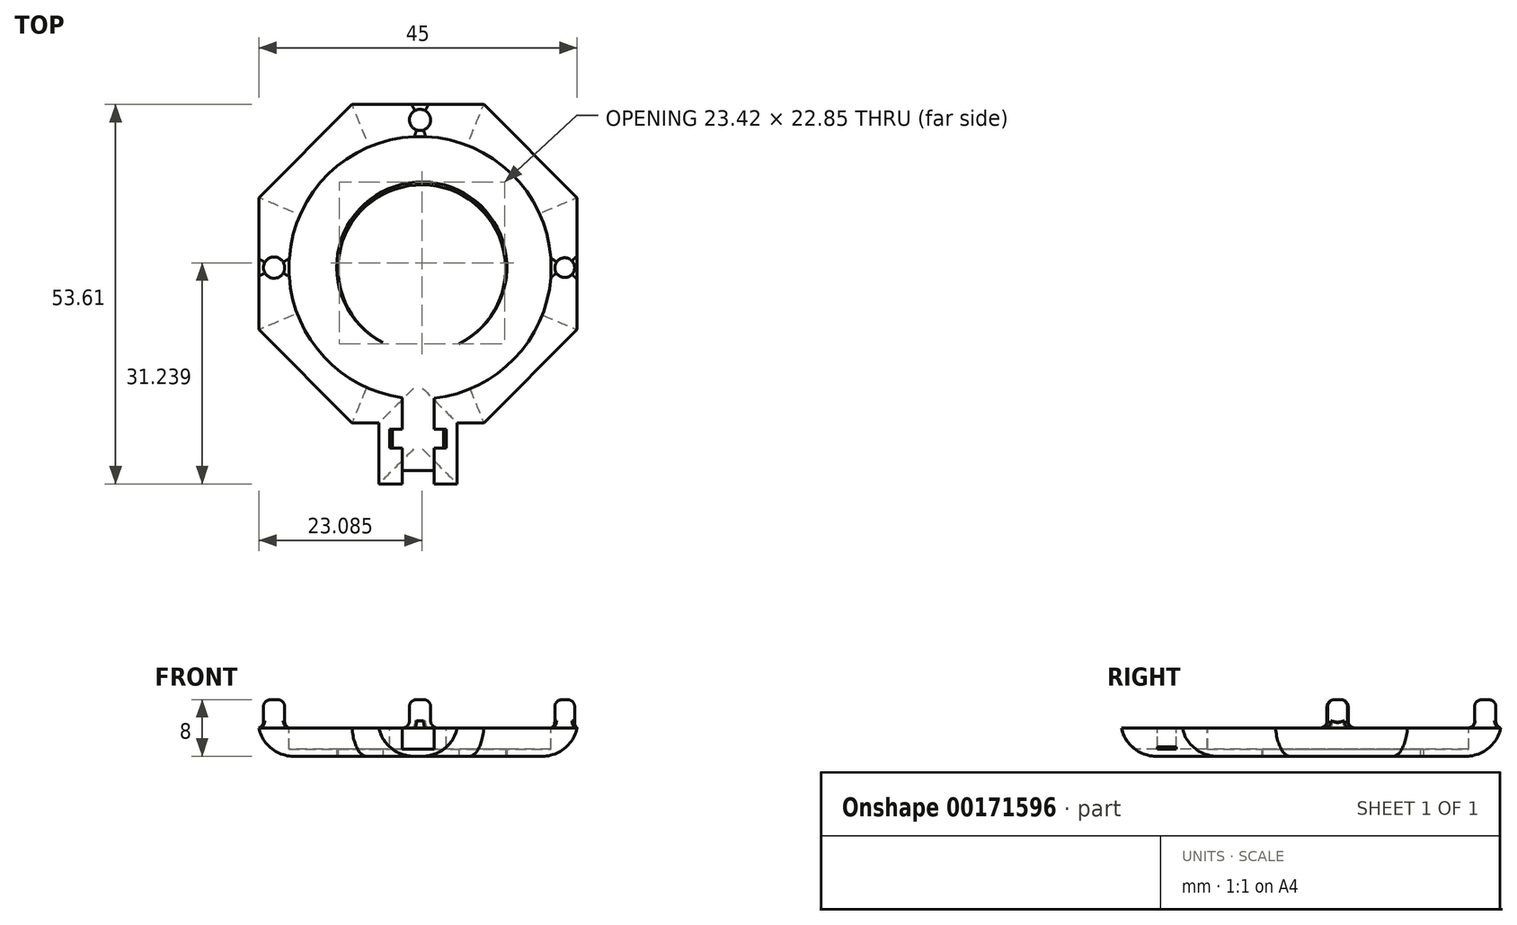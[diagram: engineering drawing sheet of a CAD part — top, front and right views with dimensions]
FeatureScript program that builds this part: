
annotation { "Feature Type Name" : "Feature", "Feature Type Description" : "" }
export const myFeature = defineFeature(function(context is Context, id is Id, definition is map)
    precondition{}
    {
        {
            var Q0;
            Q0=qCreatedBy(makeId("Top.planeOp"),FACE);
            var sketch = newSketch(context, id + "F0", { "sketchPlane" : qUnion([Q0])});
            skCircle(sketch, "E0.cCircle", {"center": v(-0.3, 0.57) * mm, "radius": 22.5 * mm, "construction": true});
            skLineSegment(sketch, "E0.0", {"start": v(9.02, -21.93) * mm, "end": v(-9.62, -21.93) * mm});
            skLineSegment(sketch, "E0.1", {"start": v(-9.62, -21.93) * mm, "end": v(-22.8, -8.75) * mm});
            skLineSegment(sketch, "E0.2", {"start": v(-22.8, -8.75) * mm, "end": v(-22.8, 9.9) * mm});
            skLineSegment(sketch, "E0.3", {"start": v(-22.8, 9.9) * mm, "end": v(-9.62, 23.07) * mm});
            skLineSegment(sketch, "E0.4", {"start": v(-9.62, 23.07) * mm, "end": v(9.02, 23.07) * mm});
            skLineSegment(sketch, "E0.5", {"start": v(9.02, 23.07) * mm, "end": v(22.2, 9.9) * mm});
            skLineSegment(sketch, "E0.6", {"start": v(22.2, 9.9) * mm, "end": v(22.2, -8.75) * mm});
            skLineSegment(sketch, "E0.7", {"start": v(22.2, -8.75) * mm, "end": v(9.02, -21.93) * mm});
            skPoint(sketch, "E0.0.midPoint", {"position": v(-0.3, -21.93) * mm});
            skLineSegment(sketch, "E1", {"start": v(5.26, -21.93) * mm, "end": v(5.26, -30.54) * mm});
            skLineSegment(sketch, "E2", {"start": v(5.26, -30.54) * mm, "end": v(-5.8, -30.54) * mm});
            skLineSegment(sketch, "E3", {"start": v(-5.8, -30.54) * mm, "end": v(-5.8, -21.93) * mm});
            skSolve(sketch);
        }
        {
            var Q0;
            Q0 = qSketchRegion(id + "F0", true);
            extrude(context, id + "F1", {"entities" : qUnion([Q0]), "depth" : 4 * mm});
        }
        {
            var Q0;
            Q0=makeQuery(id+"F1.opExtrude","CAP_FACE",FACE,{"disambiguationData":[OSD([sQuery(id+"F0.wireOp",EDGE,"E0.0"),sQuery(id+"F0.wireOp",EDGE,"E0.1"),sQuery(id+"F0.wireOp",EDGE,"E0.2"),sQuery(id+"F0.wireOp",EDGE,"E0.3"),sQuery(id+"F0.wireOp",EDGE,"E0.4"),sQuery(id+"F0.wireOp",EDGE,"E0.5"),sQuery(id+"F0.wireOp",EDGE,"E0.6"),sQuery(id+"F0.wireOp",EDGE,"E0.7")])],"isStart":false});
            var sketch = newSketch(context, id + "F2", { "sketchPlane" : qUnion([Q0])});
            skCircle(sketch, "E4", {"center": v(0, 0) * mm, "radius": 18.53 * mm});
            skLineSegment(sketch, "E5.bottom", {"start": v(-2.5, -18.36) * mm, "end": v(2, -18.36) * mm});
            skLineSegment(sketch, "E6", {"start": v(2, -18.36) * mm, "end": v(2, -30.54) * mm});
            skLineSegment(sketch, "E7", {"start": v(-2.5, -18.36) * mm, "end": v(-2.5, -30.54) * mm});
            skLineSegment(sketch, "E8", {"start": v(-2.5, -30.54) * mm, "end": v(2, -30.54) * mm});
            skSolve(sketch);
        }
        {
            var Q0;
            Q0 = qSketchRegion(id + "F2", true);
            extrude(context, id + "F3", {"entities" : qUnion([Q0]), "operationType" : NewBodyOperationType.REMOVE, "oppositeDirection" : true, "depth" : 3 * mm});
        }
        {
            var Q0;
            Q0=makeQuery(id+"F1.opExtrude","CAP_FACE",FACE,{"disambiguationData":[OSD([sQuery(id+"F0.wireOp",EDGE,"E0.0"),sQuery(id+"F0.wireOp",EDGE,"E0.1"),sQuery(id+"F0.wireOp",EDGE,"E0.2"),sQuery(id+"F0.wireOp",EDGE,"E0.3"),sQuery(id+"F0.wireOp",EDGE,"E0.4"),sQuery(id+"F0.wireOp",EDGE,"E0.5"),sQuery(id+"F0.wireOp",EDGE,"E0.6"),sQuery(id+"F0.wireOp",EDGE,"E0.7")])],"isStart":false});
            var sketch = newSketch(context, id + "F4", { "sketchPlane" : qUnion([Q0])});
            skCircle(sketch, "E9", {"center": v(0, 20.88) * mm, "radius": 1.5 * mm});
            skCircle(sketch, "E10", {"center": v(20.45, 0) * mm, "radius": 1.4 * mm});
            skCircle(sketch, "E11", {"center": v(-20.63, 0.02) * mm, "radius": 1.5 * mm});
            skSolve(sketch);
        }
        {
            var Q0;
            Q0=makeQuery(id+"F4.imprint","IMPRINT",FACE,{"disambiguationData":[TD([[makeQuery(id+"F4.imprint","IMPRINT",EDGE,{"derivedFrom":sQuery(id+"F4.wireOp",EDGE,"E9")}),1.0]])]});
            var Q1;
            Q1=makeQuery(id+"F4.imprint","IMPRINT",FACE,{"disambiguationData":[TD([[makeQuery(id+"F4.imprint","IMPRINT",EDGE,{"derivedFrom":sQuery(id+"F4.wireOp",EDGE,"E10")}),1.0]])]});
            var Q2;
            Q2=makeQuery(id+"F4.imprint","IMPRINT",FACE,{"disambiguationData":[TD([[makeQuery(id+"F4.imprint","IMPRINT",EDGE,{"derivedFrom":sQuery(id+"F4.wireOp",EDGE,"E11")}),1.0]])]});
            extrude(context, id + "F5", {"entities" : qUnion([Q0, Q1, Q2]), "operationType" : NewBodyOperationType.ADD, "depth" : 4 * mm});
        }
        {
            var Q0;
            Q0=makeQuery(id+"F1.opExtrude","CAP_EDGE",EDGE,{"disambiguationData":[OSD([sQuery(id+"F0.wireOp",EDGE,"E0.1")])],"isStart":true});
            var Q1;
            Q1=makeQuery(id+"F1.opExtrude","CAP_EDGE",EDGE,{"disambiguationData":[OSD([sQuery(id+"F0.wireOp",EDGE,"E0.0")])],"isStart":true});
            var Q2;
            Q2=makeQuery(id+"F1.opExtrude","CAP_EDGE",EDGE,{"disambiguationData":[OSD([sQuery(id+"F0.wireOp",EDGE,"E0.7")])],"isStart":true});
            var Q3;
            Q3=makeQuery(id+"F1.opExtrude","CAP_EDGE",EDGE,{"disambiguationData":[OSD([sQuery(id+"F0.wireOp",EDGE,"E0.6")])],"isStart":true});
            var Q4;
            Q4=makeQuery(id+"F1.opExtrude","CAP_FACE",FACE,{"disambiguationData":[OSD([sQuery(id+"F0.wireOp",EDGE,"E0.0"),sQuery(id+"F0.wireOp",EDGE,"E0.1"),sQuery(id+"F0.wireOp",EDGE,"E0.2"),sQuery(id+"F0.wireOp",EDGE,"E0.3"),sQuery(id+"F0.wireOp",EDGE,"E0.4"),sQuery(id+"F0.wireOp",EDGE,"E0.5"),sQuery(id+"F0.wireOp",EDGE,"E0.6"),sQuery(id+"F0.wireOp",EDGE,"E0.7")])],"isStart":true});
            fillet(context, id + "F6", {"entities" : qUnion([Q0, Q1, Q2, Q3, Q4]), "radius" : 5 * mm, "tangentPropagation" : true, "allowEdgeOverflow" : false});
        }
        {
            var Q0;
            Q0=makeQuery(id+"F5.opExtrude","CAP_FACE",FACE,{"disambiguationData":[OSD([sQuery(id+"F4.wireOp",EDGE,"E10")])],"isStart":false});
            var Q1;
            Q1=makeQuery(id+"F5.opExtrude","SWEPT_FACE",FACE,{"disambiguationData":[OSD([sQuery(id+"F4.wireOp",EDGE,"E10")])]});
            var Q2;
            Q2=makeQuery(id+"F5.opExtrude","SWEPT_FACE",FACE,{"disambiguationData":[OSD([sQuery(id+"F4.wireOp",EDGE,"E11")])]});
            var Q3;
            Q3=makeQuery(id+"F5.opExtrude","SWEPT_FACE",FACE,{"disambiguationData":[OSD([sQuery(id+"F4.wireOp",EDGE,"E9")])]});
            fillet(context, id + "F7", {"entities" : qUnion([Q0, Q1, Q2, Q3]), "radius" : 1 * mm, "tangentPropagation" : true, "allowEdgeOverflow" : false});
        }
        {
            var Q0;
            Q0=makeQuery(id+"F1.opExtrude","CAP_FACE",FACE,{"disambiguationData":[OSD([sQuery(id+"F0.wireOp",EDGE,"E0.0"),sQuery(id+"F0.wireOp",EDGE,"E0.1"),sQuery(id+"F0.wireOp",EDGE,"E0.2"),sQuery(id+"F0.wireOp",EDGE,"E0.3"),sQuery(id+"F0.wireOp",EDGE,"E0.4"),sQuery(id+"F0.wireOp",EDGE,"E0.5"),sQuery(id+"F0.wireOp",EDGE,"E0.6"),sQuery(id+"F0.wireOp",EDGE,"E0.7")])],"isStart":true});
            var sketch = newSketch(context, id + "F8", { "sketchPlane" : qUnion([Q0])});
            skPoint(sketch, "E12.startSnap0", {"position": v(-12.75, 11.87) * mm});
            skPoint(sketch, "E12.endSnap0", {"position": v(-12.75, 11.87) * mm});
            skArc(sketch, "E13", {"start": v(-5.27, 10.6) * mm, "mid": v(0.4, -12.13) * mm, "end": v(5.5, 10.73) * mm});
            skArc(sketch, "E14", {"start": v(-5.27, 10.6) * mm, "mid": v(0.4, -11.71) * mm, "end": v(5.5, 10.73) * mm});
            skSolve(sketch);
        }
        {
            var Q0;
            Q0=makeQuery(id+"F8.imprint","IMPRINT",FACE,{"disambiguationData":[TD([[makeQuery(id+"F8.imprint","IMPRINT",EDGE,{"derivedFrom":sQuery(id+"F8.wireOp",EDGE,"E12")}),1.0]])]});
            var Q1;
            Q1=makeQuery(id+"F8.imprint","IMPRINT",FACE,{"disambiguationData":[TD([[makeQuery(id+"F8.imprint","IMPRINT",EDGE,{"derivedFrom":sQuery(id+"F8.wireOp",EDGE,"E13")}),1.0]])]});
            extrude(context, id + "F9", {"entities" : qUnion([Q0, Q1]), "operationType" : NewBodyOperationType.REMOVE, "oppositeDirection" : true, "depth" : 1 * mm});
        }
        {
            var Q0;
            Q0=makeQuery(id+"F7.opFillet","SPLIT",FACE,{"disambiguationData":[OD(1.0)],"derivedFrom":makeQuery(id+"F1.opExtrude","CAP_FACE",FACE,{"disambiguationData":[OSD([sQuery(id+"F0.wireOp",EDGE,"E0.0"),sQuery(id+"F0.wireOp",EDGE,"E0.1"),sQuery(id+"F0.wireOp",EDGE,"E0.2"),sQuery(id+"F0.wireOp",EDGE,"E0.3"),sQuery(id+"F0.wireOp",EDGE,"E0.4"),sQuery(id+"F0.wireOp",EDGE,"E0.5"),sQuery(id+"F0.wireOp",EDGE,"E0.6"),sQuery(id+"F0.wireOp",EDGE,"E0.7"),sQuery(id+"F0.wireOp",EDGE,"E1"),sQuery(id+"F0.wireOp",EDGE,"E2"),sQuery(id+"F0.wireOp",EDGE,"E3")])],"isStart":false})});
            var sketch = newSketch(context, id + "F10", { "sketchPlane" : qUnion([Q0])});
            skLineSegment(sketch, "E15.bottom", {"start": v(-4.27, -22.81) * mm, "end": v(3.71, -22.81) * mm});
            skLineSegment(sketch, "E15.top", {"start": v(-4.27, -25.48) * mm, "end": v(3.71, -25.48) * mm});
            skLineSegment(sketch, "E15.left", {"start": v(-4.27, -22.81) * mm, "end": v(-4.27, -25.48) * mm});
            skLineSegment(sketch, "E15.right", {"start": v(3.71, -22.81) * mm, "end": v(3.71, -25.48) * mm});
            skSolve(sketch);
        }
        {
            var Q0;
            {var subQ0=sQuery(id+"F10.wireOp",EDGE,"E15.right");Q0=makeQuery(id+"F10.imprint","IMPRINT",FACE,{"disambiguationData":[TD([[makeQuery(id+"F10.imprint","IMPRINT",EDGE,{"derivedFrom":subQ0}),-1.0]])]});}
            var Q1;
            {var subQ0=sQuery(id+"F10.wireOp",EDGE,"E15.left");Q1=makeQuery(id+"F10.imprint","IMPRINT",FACE,{"disambiguationData":[TD([[makeQuery(id+"F10.imprint","IMPRINT",EDGE,{"derivedFrom":subQ0}),1.0]])]});}
            extrude(context, id + "F11", {"entities" : qUnion([Q0, Q1]), "operationType" : NewBodyOperationType.REMOVE, "oppositeDirection" : true, "depth" : 3 * mm});
        }
    });
